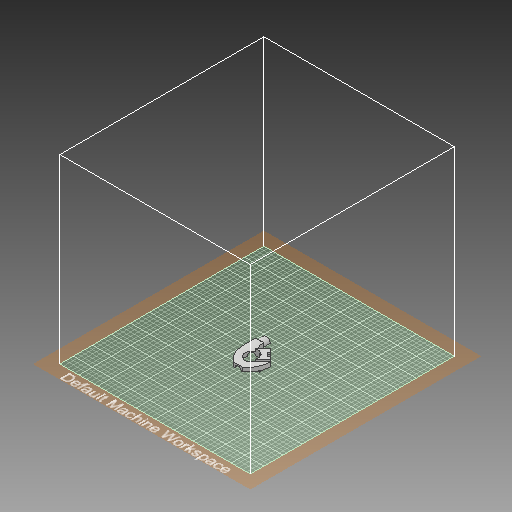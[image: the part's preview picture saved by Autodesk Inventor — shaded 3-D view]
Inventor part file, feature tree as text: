
AUTODESK INVENTOR PART (.ipt)
format: ipt  version: 2019 (Build 230136000, 136)  size: 569,344 bytes
history: native  units: mm
features: sketch x20, extrude x16, projected_geometry x3, sweep x2, other x2, fillet x1
ambient origin geometry x8: Origin, YZ Plane, XZ Plane, XY Plane, X Axis, Y Axis, Z Axis, Center Point
bodies: Body1 (feature_tree)
feature tree (44):
  extrude  "Extrusion2"  Depth=80.0mm
  sketch  "Esquisse3"
  sweep  "Balayage1"
  extrude  "Extrusion6"  Depth=32.0mm
  extrude  "Extrusion7"  Depth=18.0mm TaperAngle=0.0deg
  extrude  "Extrusion8"  TaperAngle=135.0deg  [1 undecoded]
  sketch  "Esquisse11"
  sketch  "Esquisse12"
  other  "Plan de construction1"
  sketch  "Esquisse13"
  extrude  "Extrusion9"  Depth=23.0mm
  extrude  "Extrusion10"  Depth=14.0mm
  other  "Plan de construction2"
  sketch  "Esquisse14"
  extrude  "Extrusion11"  Depth=4.0mm
  extrude  "Extrusion12"  TaperAngle=0.0deg  [1 undecoded]
  extrude  "Extrusion13"  Depth=4.0mm TaperAngle=0.0deg
  extrude  "Extrusion14"  Depth=9.0mm
  extrude  "Extrusion15"  Depth=4.0mm TaperAngle=0.0deg
  sketch  "Esquisse20"
  sketch  "Esquisse21"
  sketch  "Esquisse24"
  extrude  "Extrusion17"  Depth=2.0mm
  sweep  "Balayage4"
  extrude  "Extrusion18"  Depth=35.0mm
  extrude  "Extrusion19"  Depth=17.5mm
  extrude  "Extrusion20"  Depth=8.5mm
  extrude  "Extrusion21"  Depth=12.0mm TaperAngle=0.0deg
  fillet  "Congé1"  Radius=30.0mm
  sketch  "Esquisse2"
  sketch  "Esquisse4"
  sketch  "Esquisse8"
  sketch  "Esquisse9"
  sketch  "Esquisse10"
  sketch  "Esquisse16"
  projected_geometry  "Boucle projetée3"
  sketch  "Esquisse18"
  sketch  "Esquisse19"
  projected_geometry  "Boucle projetée4"
  projected_geometry  "Boucle projetée6"
  sketch  "Esquisse25"
  sketch  "Esquisse26"
  sketch  "Esquisse27"
  sketch  "Esquisse28"
note: 2 required parameter values undecoded (feature->parameter linkage not recoverable at this tier; creation-order binding heuristic only, values carry confidence <= 0.55)
